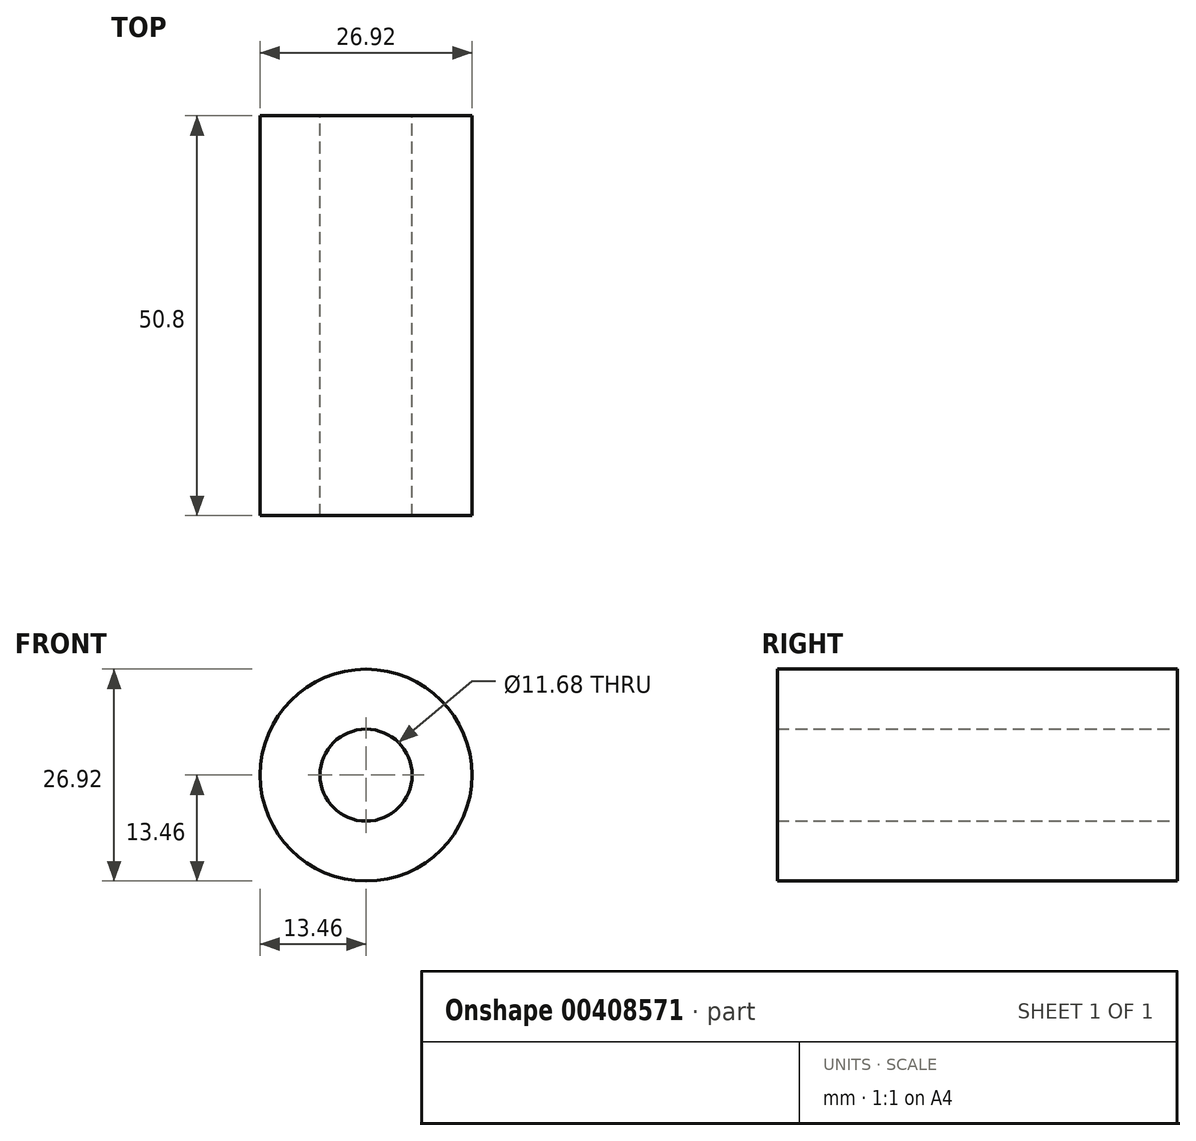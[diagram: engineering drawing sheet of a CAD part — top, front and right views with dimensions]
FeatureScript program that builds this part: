
annotation { "Feature Type Name" : "Feature", "Feature Type Description" : "" }
export const myFeature = defineFeature(function(context is Context, id is Id, definition is map)
    precondition{}
    {
        {
            var Q0;
            Q0=qCreatedBy(makeId("Front.planeOp"),FACE);
            var sketch = newSketch(context, id + "F0", { "sketchPlane" : qUnion([Q0])});
            skCircle(sketch, "E0", {"center": v(0, 0) * mm, "radius": 13.46 * mm});
            skCircle(sketch, "E1.0", {"center": v(0, 0) * mm, "radius": 5.84 * mm});
            skSolve(sketch);
        }
        {
            var Q0;
            Q0=makeQuery(id+"F0.imprint","IMPRINT",FACE,{"disambiguationData":[TD([[makeQuery(id+"F0.imprint","IMPRINT",EDGE,{"derivedFrom":sQuery(id+"F0.wireOp",EDGE,"E0")}),1.0]])]});
            extrude(context, id + "F1", {"entities" : qUnion([Q0]), "depth" : 50.8 * mm});
        }
    });
